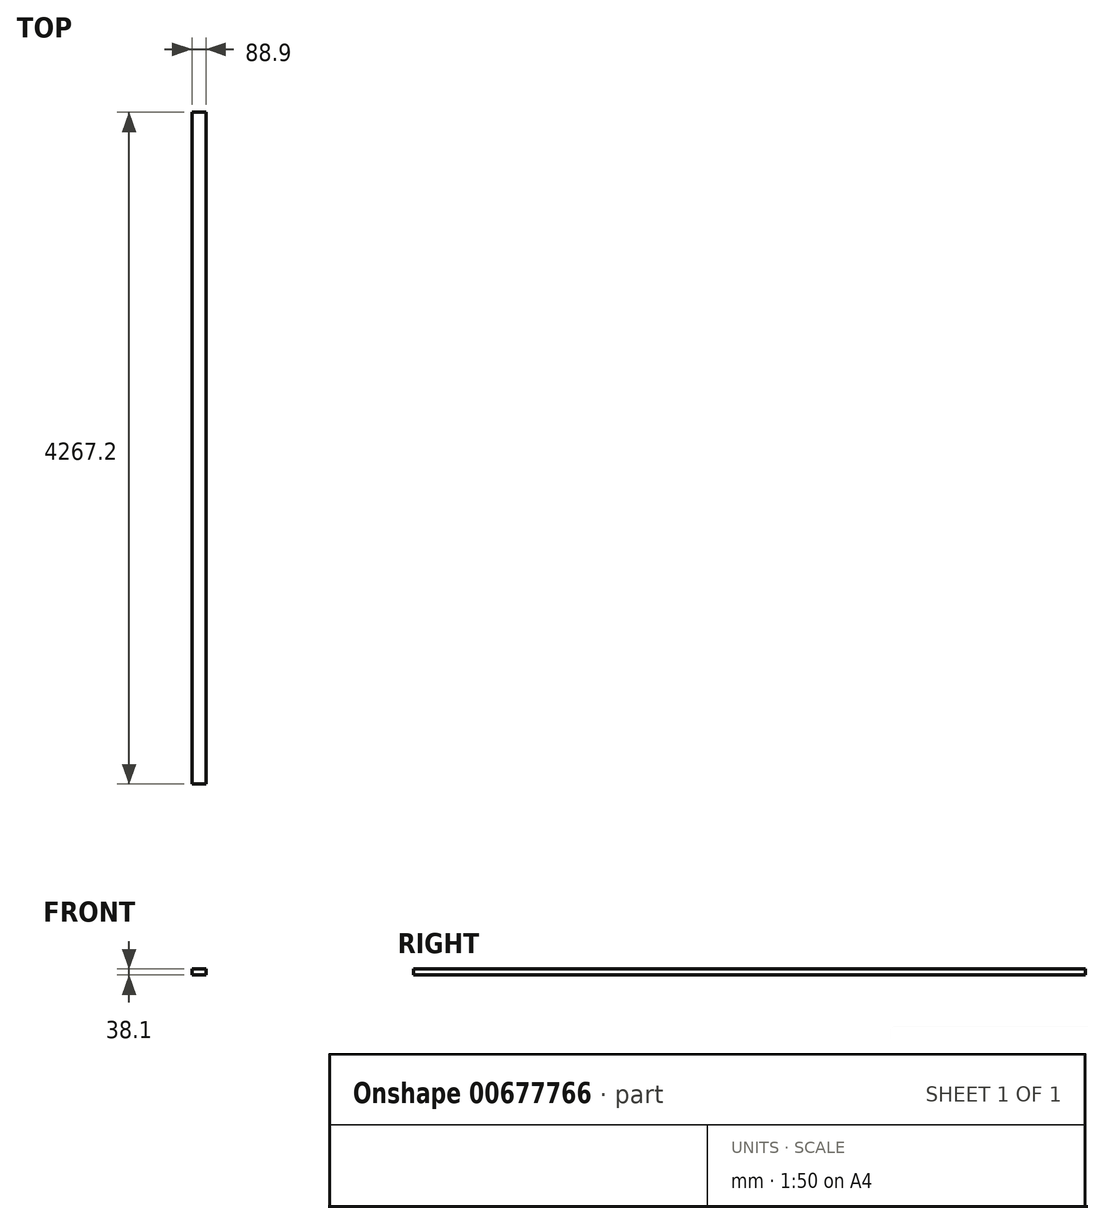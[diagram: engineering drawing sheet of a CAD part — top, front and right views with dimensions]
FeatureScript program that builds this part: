
annotation { "Feature Type Name" : "Feature", "Feature Type Description" : "" }
export const myFeature = defineFeature(function(context is Context, id is Id, definition is map)
    precondition{}
    {
        {
            var Q0;
            Q0=qCreatedBy(makeId("Front.planeOp"),FACE);
            var sketch = newSketch(context, id + "F0", { "sketchPlane" : qUnion([Q0])});
            skLineSegment(sketch, "E0.bottom", {"start": v(1392.05, -244.34) * mm, "end": v(1480.95, -244.34) * mm});
            skLineSegment(sketch, "E0.top", {"start": v(1392.05, -206.24) * mm, "end": v(1480.95, -206.24) * mm});
            skLineSegment(sketch, "E0.left", {"start": v(1392.05, -244.34) * mm, "end": v(1392.05, -206.24) * mm});
            skLineSegment(sketch, "E0.right", {"start": v(1480.95, -244.34) * mm, "end": v(1480.95, -206.24) * mm});
            skSolve(sketch);
        }
        {
            var Q0;
            Q0=makeQuery(id+"F0.imprint","IMPRINT",FACE,{"disambiguationData":[TD([[makeQuery(id+"F0.imprint","IMPRINT",EDGE,{"derivedFrom":sQuery(id+"F0.wireOp",EDGE,"E0.bottom")}),1.0]])]});
            extrude(context, id + "F1", {"entities" : qUnion([Q0]), "depth" : 4267.2 * mm, "offsetDistance" : 25.4 * mm});
        }
    });
